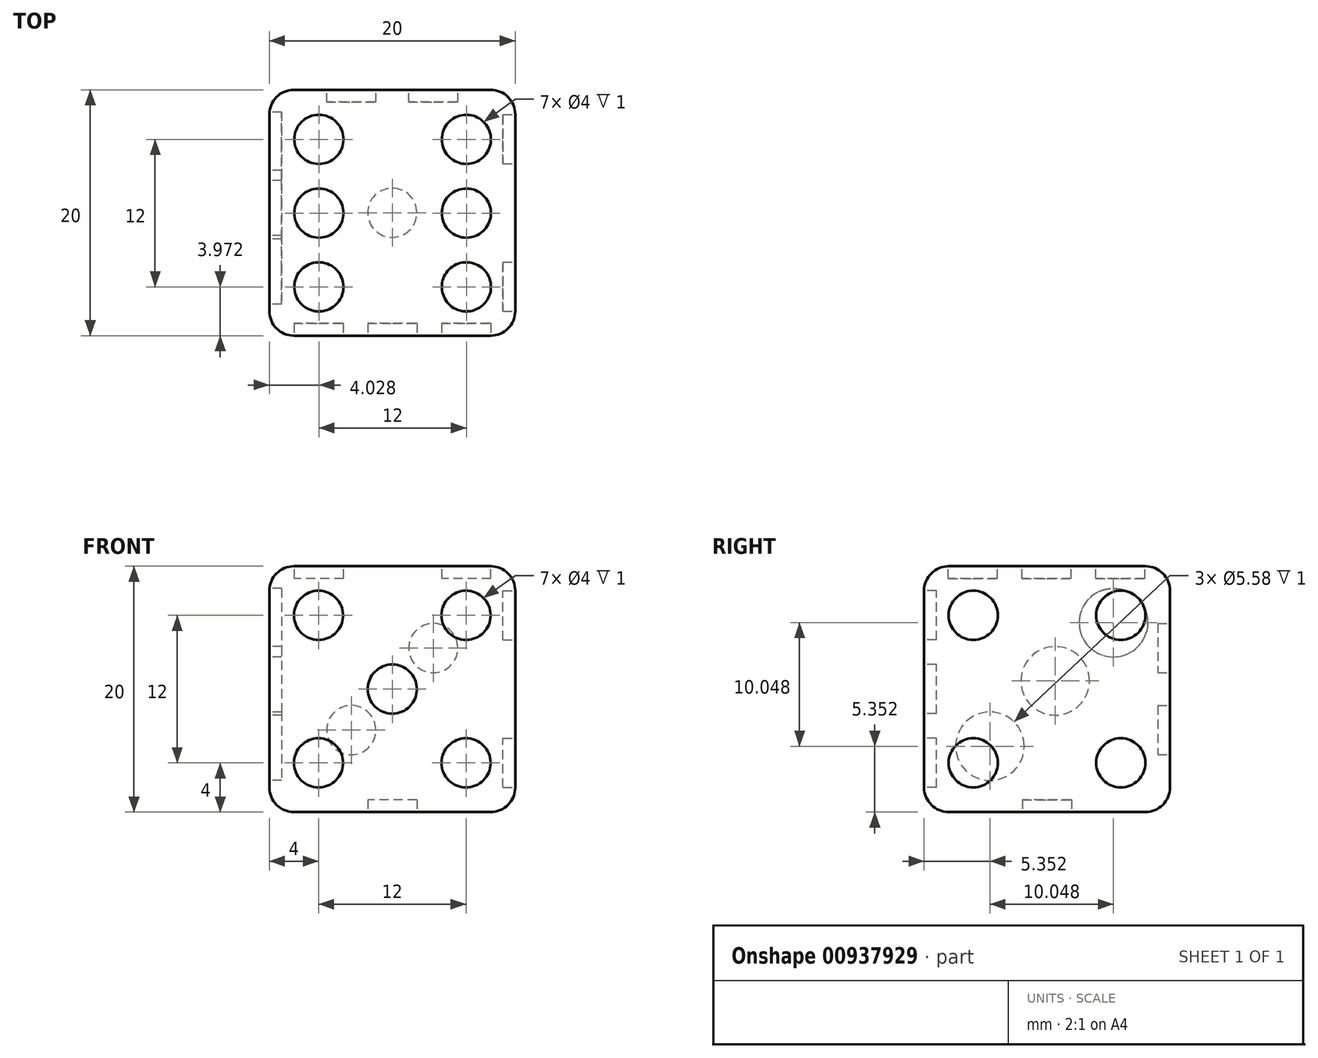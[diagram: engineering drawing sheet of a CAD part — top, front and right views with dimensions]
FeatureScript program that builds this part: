
annotation { "Feature Type Name" : "Feature", "Feature Type Description" : "" }
export const myFeature = defineFeature(function(context is Context, id is Id, definition is map)
    precondition{}
    {
        {
            var Q0;
            Q0=qCreatedBy(makeId("Top.planeOp"),FACE);
            var sketch = newSketch(context, id + "F0", { "sketchPlane" : qUnion([Q0])});
            skLineSegment(sketch, "E0.bottom", {"start": v(0, 0) * mm, "end": v(20, 0) * mm});
            skLineSegment(sketch, "E0.top", {"start": v(0, 20) * mm, "end": v(20, 20) * mm});
            skLineSegment(sketch, "E0.left", {"start": v(0, 0) * mm, "end": v(0, 20) * mm});
            skLineSegment(sketch, "E0.right", {"start": v(20, 0) * mm, "end": v(20, 20) * mm});
            skSolve(sketch);
        }
        {
            var Q0;
            Q0 = qSketchRegion(id + "F0", true);
            extrude(context, id + "F1", {"entities" : qUnion([Q0]), "depth" : 20 * mm, "offsetDistance" : 25 * mm});
        }
        {
            var Q0;
            Q0=qCreatedBy(makeId("Top.planeOp"),FACE);
            var sketch = newSketch(context, id + "F2", { "sketchPlane" : qUnion([Q0])});
            skCircle(sketch, "E1", {"center": v(10, 10) * mm, "radius": 2 * mm});
            skLineSegment(sketch, "E2.0.0", {"start": v(20, 20) * mm, "end": v(0, 20) * mm});
            skLineSegment(sketch, "E2.0.1", {"start": v(0, 20) * mm, "end": v(0, 0) * mm});
            skLineSegment(sketch, "E2.0.2", {"start": v(0, 0) * mm, "end": v(20, 0) * mm});
            skLineSegment(sketch, "E2.0.3", {"start": v(20, 0) * mm, "end": v(20, 20) * mm});
            skLineSegment(sketch, "E3", {"start": v(20, 20) * mm, "end": v(0, 0) * mm, "construction": true});
            skLineSegment(sketch, "E4", {"start": v(0, 20) * mm, "end": v(20, 0) * mm, "construction": true});
            skSolve(sketch);
        }
        {
            var Q0;
            Q0=makeQuery(id+"F1.opExtrude","CAP_FACE",FACE,{"disambiguationData":[OSD([sQuery(id+"F0.wireOp",EDGE,"E0.bottom"),sQuery(id+"F0.wireOp",EDGE,"E0.top"),sQuery(id+"F0.wireOp",EDGE,"E0.left"),sQuery(id+"F0.wireOp",EDGE,"E0.right")])],"isStart":false});
            var sketch = newSketch(context, id + "F3", { "sketchPlane" : qUnion([Q0])});
            skLineSegment(sketch, "E5", {"start": v(20, 20) * mm, "end": v(0, 0) * mm, "construction": true});
            skLineSegment(sketch, "E6", {"start": v(0, 20) * mm, "end": v(20, 0) * mm, "construction": true});
            skLineSegment(sketch, "E7.bottom", {"start": v(4.03, 15.97) * mm, "end": v(16.03, 15.97) * mm, "construction": true});
            skLineSegment(sketch, "E7.top", {"start": v(4.03, 3.97) * mm, "end": v(16.03, 3.97) * mm, "construction": true});
            skLineSegment(sketch, "E7.left", {"start": v(4.03, 15.97) * mm, "end": v(4.03, 3.97) * mm, "construction": true});
            skLineSegment(sketch, "E7.right", {"start": v(16.03, 15.97) * mm, "end": v(16.03, 3.97) * mm, "construction": true});
            skCircle(sketch, "E8", {"center": v(4.03, 15.97) * mm, "radius": 2 * mm});
            skCircle(sketch, "E9", {"center": v(4.03, 3.97) * mm, "radius": 2 * mm});
            skCircle(sketch, "E10", {"center": v(16.03, 3.97) * mm, "radius": 2 * mm});
            skCircle(sketch, "E11", {"center": v(16.03, 15.97) * mm, "radius": 2 * mm});
            skCircle(sketch, "E12", {"center": v(16.03, 9.97) * mm, "radius": 2 * mm});
            skCircle(sketch, "E13", {"center": v(4.03, 9.97) * mm, "radius": 2 * mm});
            skSolve(sketch);
        }
        {
            var Q0;
            Q0=qCreatedBy(makeId("Front.planeOp"),FACE);
            var sketch = newSketch(context, id + "F4", { "sketchPlane" : qUnion([Q0])});
            skLineSegment(sketch, "E14", {"start": v(20, 0) * mm, "end": v(0, 20) * mm, "construction": true});
            skLineSegment(sketch, "E15", {"start": v(0, 0) * mm, "end": v(20, 20) * mm, "construction": true});
            skLineSegment(sketch, "E16.bottom", {"start": v(16, 16) * mm, "end": v(4, 16) * mm, "construction": true});
            skLineSegment(sketch, "E16.top", {"start": v(16, 4) * mm, "end": v(4, 4) * mm, "construction": true});
            skLineSegment(sketch, "E16.left", {"start": v(16, 16) * mm, "end": v(16, 4) * mm, "construction": true});
            skLineSegment(sketch, "E16.right", {"start": v(4, 16) * mm, "end": v(4, 4) * mm, "construction": true});
            skCircle(sketch, "E17", {"center": v(16, 4) * mm, "radius": 2 * mm});
            skCircle(sketch, "E18", {"center": v(4, 16) * mm, "radius": 2 * mm});
            skCircle(sketch, "E19", {"center": v(16, 16) * mm, "radius": 2 * mm});
            skCircle(sketch, "E20", {"center": v(4, 4) * mm, "radius": 2 * mm});
            skCircle(sketch, "E21", {"center": v(10, 10) * mm, "radius": 2 * mm});
            skSolve(sketch);
        }
        {
            var Q0;
            Q0=makeQuery(id+"F1.opExtrude","SWEPT_FACE",FACE,{"disambiguationData":[OSD([sQuery(id+"F0.wireOp",EDGE,"E0.top")])]});
            var sketch = newSketch(context, id + "F5", { "sketchPlane" : qUnion([Q0])});
            skCircle(sketch, "E22", {"center": v(-13.33, 13.33) * mm, "radius": 2 * mm});
            skCircle(sketch, "E23", {"center": v(-6.67, 6.67) * mm, "radius": 2 * mm});
            skLineSegment(sketch, "E24", {"start": v(-20, 20) * mm, "end": v(-13.33, 13.33) * mm, "construction": true});
            skLineSegment(sketch, "E25", {"start": v(-13.33, 13.33) * mm, "end": v(-6.67, 6.67) * mm, "construction": true});
            skLineSegment(sketch, "E26", {"start": v(-6.67, 6.67) * mm, "end": v(0, 0) * mm, "construction": true});
            skSolve(sketch);
        }
        {
            var Q0;
            Q0=makeQuery(id+"F1.opExtrude","SWEPT_FACE",FACE,{"disambiguationData":[OSD([sQuery(id+"F0.wireOp",EDGE,"E0.left")])]});
            var sketch = newSketch(context, id + "F6", { "sketchPlane" : qUnion([Q0])});
            skCircle(sketch, "E27", {"center": v(-15.4, 15.4) * mm, "radius": 2.79 * mm});
            skCircle(sketch, "E28", {"center": v(-10.67, 10.67) * mm, "radius": 2.79 * mm});
            skCircle(sketch, "E29", {"center": v(-5.35, 5.35) * mm, "radius": 2.79 * mm});
            skLineSegment(sketch, "E30", {"start": v(-20, 20) * mm, "end": v(-15.4, 15.4) * mm, "construction": true});
            skLineSegment(sketch, "E31", {"start": v(-15.4, 15.4) * mm, "end": v(-10.67, 10.67) * mm, "construction": true});
            skLineSegment(sketch, "E32", {"start": v(-10.67, 10.67) * mm, "end": v(-5.35, 5.35) * mm, "construction": true});
            skLineSegment(sketch, "E33", {"start": v(-5.35, 5.35) * mm, "end": v(0, 0) * mm, "construction": true});
            skSolve(sketch);
        }
        {
            var Q0;
            Q0=makeQuery(id+"F1.opExtrude","SWEPT_FACE",FACE,{"disambiguationData":[OSD([sQuery(id+"F0.wireOp",EDGE,"E0.right")])]});
            var sketch = newSketch(context, id + "F7", { "sketchPlane" : qUnion([Q0])});
            skLineSegment(sketch, "E34", {"start": v(20, 20) * mm, "end": v(0, 0) * mm, "construction": true});
            skLineSegment(sketch, "E35", {"start": v(0, 20) * mm, "end": v(20, 0) * mm, "construction": true});
            skLineSegment(sketch, "E36.bottom", {"start": v(4, 16) * mm, "end": v(16, 16) * mm, "construction": true});
            skLineSegment(sketch, "E36.top", {"start": v(4, 4) * mm, "end": v(16, 4) * mm, "construction": true});
            skLineSegment(sketch, "E36.left", {"start": v(4, 16) * mm, "end": v(4, 4) * mm, "construction": true});
            skLineSegment(sketch, "E36.right", {"start": v(16, 16) * mm, "end": v(16, 4) * mm, "construction": true});
            skCircle(sketch, "E37", {"center": v(4, 16) * mm, "radius": 2 * mm});
            skCircle(sketch, "E38", {"center": v(4, 4) * mm, "radius": 2 * mm});
            skCircle(sketch, "E39", {"center": v(16, 4) * mm, "radius": 2 * mm});
            skCircle(sketch, "E40", {"center": v(16, 16) * mm, "radius": 2 * mm});
            skSolve(sketch);
        }
        {
            var Q0;
            Q0=makeQuery(id+"F3.imprint","IMPRINT",FACE,{"disambiguationData":[TD([[makeQuery(id+"F3.imprint","IMPRINT",EDGE,{"derivedFrom":sQuery(id+"F3.wireOp",EDGE,"E8")}),1.0]])]});
            var Q1;
            Q1=makeQuery(id+"F3.imprint","IMPRINT",FACE,{"disambiguationData":[TD([[makeQuery(id+"F3.imprint","IMPRINT",EDGE,{"derivedFrom":sQuery(id+"F3.wireOp",EDGE,"E13")}),1.0]])]});
            var Q2;
            Q2=makeQuery(id+"F3.imprint","IMPRINT",FACE,{"disambiguationData":[TD([[makeQuery(id+"F3.imprint","IMPRINT",EDGE,{"derivedFrom":sQuery(id+"F3.wireOp",EDGE,"E9")}),1.0]])]});
            var Q3;
            Q3=makeQuery(id+"F3.imprint","IMPRINT",FACE,{"disambiguationData":[TD([[makeQuery(id+"F3.imprint","IMPRINT",EDGE,{"derivedFrom":sQuery(id+"F3.wireOp",EDGE,"E11")}),1.0]])]});
            var Q4;
            Q4=makeQuery(id+"F3.imprint","IMPRINT",FACE,{"disambiguationData":[TD([[makeQuery(id+"F3.imprint","IMPRINT",EDGE,{"derivedFrom":sQuery(id+"F3.wireOp",EDGE,"E12")}),1.0]])]});
            var Q5;
            Q5=makeQuery(id+"F3.imprint","IMPRINT",FACE,{"disambiguationData":[TD([[makeQuery(id+"F3.imprint","IMPRINT",EDGE,{"derivedFrom":sQuery(id+"F3.wireOp",EDGE,"E10")}),1.0]])]});
            extrude(context, id + "F8", {"entities" : qUnion([Q0, Q1, Q2, Q3, Q4, Q5]), "operationType" : NewBodyOperationType.REMOVE, "oppositeDirection" : true, "depth" : 1 * mm, "offsetDistance" : 25 * mm});
        }
        {
            var Q0;
            {var subQ0=sQuery(id+"F2.wireOp",EDGE,"DLmDA1Jz-B1Br-PbYC-twxk-7bfob2sfivJC");var subQ1=sQuery(id+"F2.wireOp",EDGE,"E1");var subQ2=makeQuery(id+"F2.imprint","INTERSECT",VERTEX,{"disambiguationData":[OD(0.0)],"derivedFrom":[subQ1,subQ0]});Q0=makeQuery(id+"F2.imprint","IMPRINT",FACE,{"disambiguationData":[TD([[makeQuery(id+"F2.imprint","IMPRINT",EDGE,{"disambiguationData":[TD([[subQ2,1.0]])],"derivedFrom":subQ1}),1.0]])]});}
            var Q1;
            {var subQ0=sQuery(id+"F2.wireOp",EDGE,"DLmDA1Jz-B1Br-PbYC-twxk-7bfob2sfivJC");var subQ1=sQuery(id+"F2.wireOp",EDGE,"E1");var subQ2=makeQuery(id+"F2.imprint","INTERSECT",VERTEX,{"disambiguationData":[OD(0.0)],"derivedFrom":[subQ1,subQ0]});Q1=makeQuery(id+"F2.imprint","IMPRINT",FACE,{"disambiguationData":[TD([[makeQuery(id+"F2.imprint","IMPRINT",EDGE,{"disambiguationData":[TD([[subQ2,-1.0]])],"derivedFrom":subQ1}),1.0]])]});}
            var Q2;
            {var subQ0=sQuery(id+"F2.wireOp",EDGE,"LqWkyFCt-tRJL-dN5y-AN8d-2VUP0lAdGxYt");var subQ1=sQuery(id+"F2.wireOp",EDGE,"E1");var subQ2=makeQuery(id+"F2.imprint","INTERSECT",VERTEX,{"disambiguationData":[OD(0.0)],"derivedFrom":[subQ1,subQ0]});Q2=makeQuery(id+"F2.imprint","IMPRINT",FACE,{"disambiguationData":[TD([[makeQuery(id+"F2.imprint","IMPRINT",EDGE,{"disambiguationData":[TD([[subQ2,1.0]])],"derivedFrom":subQ1}),1.0]])]});}
            var Q3;
            {var subQ0=sQuery(id+"F2.wireOp",EDGE,"LqWkyFCt-tRJL-dN5y-AN8d-2VUP0lAdGxYt");var subQ1=sQuery(id+"F2.wireOp",EDGE,"E1");var subQ2=makeQuery(id+"F2.imprint","INTERSECT",VERTEX,{"disambiguationData":[OD(1.0)],"derivedFrom":[subQ1,subQ0]});Q3=makeQuery(id+"F2.imprint","IMPRINT",FACE,{"disambiguationData":[TD([[makeQuery(id+"F2.imprint","IMPRINT",EDGE,{"disambiguationData":[TD([[subQ2,-1.0]])],"derivedFrom":subQ1}),1.0]])]});}
            var Q4;
            Q4=sQuery(id+"F2.wireOp",EDGE,"E1");
            extrude(context, id + "F9", {"entities" : qUnion([Q0, Q1, Q2, Q3]), "operationType" : NewBodyOperationType.REMOVE, "surfaceEntities" : qUnion([Q4]), "oppositeDirection" : true, "depth" : 1 * mm, "offsetDistance" : 25 * mm});
        }
        {
            var Q0;
            {var subQ0=sQuery(id+"F2.wireOp",EDGE,"LqWkyFCt-tRJL-dN5y-AN8d-2VUP0lAdGxYt");var subQ1=sQuery(id+"F2.wireOp",EDGE,"E1");var subQ2=makeQuery(id+"F2.imprint","INTERSECT",VERTEX,{"disambiguationData":[OD(0.0)],"derivedFrom":[subQ1,subQ0]});Q0=makeQuery(id+"F2.imprint","IMPRINT",FACE,{"disambiguationData":[TD([[makeQuery(id+"F2.imprint","IMPRINT",EDGE,{"disambiguationData":[TD([[subQ2,1.0]])],"derivedFrom":subQ1}),1.0]])]});}
            var Q1;
            {var subQ0=sQuery(id+"F2.wireOp",EDGE,"DLmDA1Jz-B1Br-PbYC-twxk-7bfob2sfivJC");var subQ1=sQuery(id+"F2.wireOp",EDGE,"E1");var subQ2=makeQuery(id+"F2.imprint","INTERSECT",VERTEX,{"disambiguationData":[OD(0.0)],"derivedFrom":[subQ1,subQ0]});Q1=makeQuery(id+"F2.imprint","IMPRINT",FACE,{"disambiguationData":[TD([[makeQuery(id+"F2.imprint","IMPRINT",EDGE,{"disambiguationData":[TD([[subQ2,1.0]])],"derivedFrom":subQ1}),1.0]])]});}
            var Q2;
            {var subQ0=sQuery(id+"F2.wireOp",EDGE,"LqWkyFCt-tRJL-dN5y-AN8d-2VUP0lAdGxYt");var subQ1=sQuery(id+"F2.wireOp",EDGE,"E1");var subQ2=makeQuery(id+"F2.imprint","INTERSECT",VERTEX,{"disambiguationData":[OD(1.0)],"derivedFrom":[subQ1,subQ0]});Q2=makeQuery(id+"F2.imprint","IMPRINT",FACE,{"disambiguationData":[TD([[makeQuery(id+"F2.imprint","IMPRINT",EDGE,{"disambiguationData":[TD([[subQ2,-1.0]])],"derivedFrom":subQ1}),1.0]])]});}
            var Q3;
            {var subQ0=sQuery(id+"F2.wireOp",EDGE,"DLmDA1Jz-B1Br-PbYC-twxk-7bfob2sfivJC");var subQ1=sQuery(id+"F2.wireOp",EDGE,"E1");var subQ2=makeQuery(id+"F2.imprint","INTERSECT",VERTEX,{"disambiguationData":[OD(0.0)],"derivedFrom":[subQ1,subQ0]});Q3=makeQuery(id+"F2.imprint","IMPRINT",FACE,{"disambiguationData":[TD([[makeQuery(id+"F2.imprint","IMPRINT",EDGE,{"disambiguationData":[TD([[subQ2,-1.0]])],"derivedFrom":subQ1}),1.0]])]});}
            var Q4;
            Q4=sQuery(id+"F2.wireOp",EDGE,"E1");
            extrude(context, id + "F10", {"entities" : qUnion([Q0, Q1, Q2, Q3]), "operationType" : NewBodyOperationType.REMOVE, "surfaceEntities" : qUnion([Q4]), "oppositeDirection" : true, "depth" : 1 * mm, "offsetDistance" : 25 * mm});
        }
        {
            var Q0;
            Q0=makeQuery(id+"F2.imprint","IMPRINT",FACE,{"disambiguationData":[TD([[makeQuery(id+"F2.imprint","IMPRINT",EDGE,{"derivedFrom":sQuery(id+"F2.wireOp",EDGE,"E1")}),1.0]])]});
            extrude(context, id + "F11", {"entities" : qUnion([Q0]), "operationType" : NewBodyOperationType.REMOVE, "depth" : 1 * mm, "offsetDistance" : 25 * mm});
        }
        {
            var Q0;
            Q0=makeQuery(id+"F6.imprint","IMPRINT",FACE,{"disambiguationData":[TD([[makeQuery(id+"F6.imprint","IMPRINT",EDGE,{"derivedFrom":sQuery(id+"F6.wireOp",EDGE,"E27")}),1.0]])]});
            var Q1;
            Q1=makeQuery(id+"F6.imprint","IMPRINT",FACE,{"disambiguationData":[TD([[makeQuery(id+"F6.imprint","IMPRINT",EDGE,{"derivedFrom":sQuery(id+"F6.wireOp",EDGE,"E28")}),1.0]])]});
            var Q2;
            Q2=makeQuery(id+"F6.imprint","IMPRINT",FACE,{"disambiguationData":[TD([[makeQuery(id+"F6.imprint","IMPRINT",EDGE,{"derivedFrom":sQuery(id+"F6.wireOp",EDGE,"E29")}),1.0]])]});
            extrude(context, id + "F12", {"entities" : qUnion([Q0, Q1, Q2]), "operationType" : NewBodyOperationType.REMOVE, "oppositeDirection" : true, "depth" : 1 * mm, "offsetDistance" : 25 * mm});
        }
        {
            var Q0;
            Q0 = qSketchRegion(id + "F4", true);
            extrude(context, id + "F13", {"entities" : qUnion([Q0]), "operationType" : NewBodyOperationType.REMOVE, "oppositeDirection" : true, "depth" : 1 * mm, "offsetDistance" : 25 * mm});
        }
        {
            var Q0;
            Q0=makeQuery(id+"F6.imprint","IMPRINT",FACE,{"disambiguationData":[TD([[makeQuery(id+"F6.imprint","IMPRINT",EDGE,{"derivedFrom":sQuery(id+"F6.wireOp",EDGE,"E27")}),1.0]])]});
            var Q1;
            Q1=makeQuery(id+"F6.imprint","IMPRINT",FACE,{"disambiguationData":[TD([[makeQuery(id+"F6.imprint","IMPRINT",EDGE,{"derivedFrom":sQuery(id+"F6.wireOp",EDGE,"E28")}),1.0]])]});
            var Q2;
            Q2=makeQuery(id+"F6.imprint","IMPRINT",FACE,{"disambiguationData":[TD([[makeQuery(id+"F6.imprint","IMPRINT",EDGE,{"derivedFrom":sQuery(id+"F6.wireOp",EDGE,"E29")}),1.0]])]});
            var Q3;
            Q3=sQuery(id+"F6.wireOp",EDGE,"E27");
            var Q4;
            Q4=sQuery(id+"F6.wireOp",EDGE,"E28");
            var Q5;
            Q5=sQuery(id+"F6.wireOp",EDGE,"E29");
            extrude(context, id + "F14", {"entities" : qUnion([Q0, Q1, Q2]), "operationType" : NewBodyOperationType.REMOVE, "surfaceEntities" : qUnion([Q3, Q4, Q5]), "oppositeDirection" : true, "depth" : 1 * mm, "offsetDistance" : 25 * mm});
        }
        {
            var Q0;
            Q0 = qSketchRegion(id + "F5", true);
            extrude(context, id + "F15", {"entities" : qUnion([Q0]), "operationType" : NewBodyOperationType.REMOVE, "oppositeDirection" : true, "depth" : 1 * mm, "offsetDistance" : 25 * mm});
        }
        {
            var Q0;
            Q0=makeQuery(id+"F7.imprint","IMPRINT",FACE,{"disambiguationData":[TD([[makeQuery(id+"F7.imprint","IMPRINT",EDGE,{"derivedFrom":sQuery(id+"F7.wireOp",EDGE,"E39")}),1.0]])]});
            var Q1;
            Q1=makeQuery(id+"F7.imprint","IMPRINT",FACE,{"disambiguationData":[TD([[makeQuery(id+"F7.imprint","IMPRINT",EDGE,{"derivedFrom":sQuery(id+"F7.wireOp",EDGE,"E40")}),1.0]])]});
            var Q2;
            Q2=makeQuery(id+"F7.imprint","IMPRINT",FACE,{"disambiguationData":[TD([[makeQuery(id+"F7.imprint","IMPRINT",EDGE,{"derivedFrom":sQuery(id+"F7.wireOp",EDGE,"E37")}),1.0]])]});
            var Q3;
            Q3=makeQuery(id+"F7.imprint","IMPRINT",FACE,{"disambiguationData":[TD([[makeQuery(id+"F7.imprint","IMPRINT",EDGE,{"derivedFrom":sQuery(id+"F7.wireOp",EDGE,"E38")}),1.0]])]});
            extrude(context, id + "F16", {"entities" : qUnion([Q0, Q1, Q2, Q3]), "operationType" : NewBodyOperationType.REMOVE, "oppositeDirection" : true, "depth" : 1 * mm, "offsetDistance" : 25 * mm});
        }
        {
            var Q0;
            Q0=makeQuery(id+"F1.opExtrude","CAP_EDGE",EDGE,{"disambiguationData":[OSD([sQuery(id+"F0.wireOp",EDGE,"E0.top")])],"isStart":true});
            var Q1;
            Q1=makeQuery(id+"F1.opExtrude","CAP_EDGE",EDGE,{"disambiguationData":[OSD([sQuery(id+"F0.wireOp",EDGE,"E0.right")])],"isStart":true});
            var Q2;
            Q2=makeQuery(id+"F1.opExtrude","CAP_EDGE",EDGE,{"disambiguationData":[OSD([sQuery(id+"F0.wireOp",EDGE,"E0.bottom")])],"isStart":true});
            var Q3;
            Q3=makeQuery(id+"F1.opExtrude","CAP_EDGE",EDGE,{"disambiguationData":[OSD([sQuery(id+"F0.wireOp",EDGE,"E0.left")])],"isStart":true});
            var Q4;
            Q4=makeQuery(id+"F1.opExtrude","SWEPT_EDGE",EDGE,{"disambiguationData":[OSD([sQuery(id+"F0.wireOp",EDGE,"E0.bottom"),sQuery(id+"F0.wireOp",EDGE,"E0.left")])]});
            var Q5;
            Q5=makeQuery(id+"F1.opExtrude","CAP_EDGE",EDGE,{"disambiguationData":[OSD([sQuery(id+"F0.wireOp",EDGE,"E0.left")])],"isStart":false});
            var Q6;
            Q6=makeQuery(id+"F1.opExtrude","SWEPT_EDGE",EDGE,{"disambiguationData":[OSD([sQuery(id+"F0.wireOp",EDGE,"E0.top"),sQuery(id+"F0.wireOp",EDGE,"E0.left")])]});
            var Q7;
            Q7=makeQuery(id+"F1.opExtrude","CAP_EDGE",EDGE,{"disambiguationData":[OSD([sQuery(id+"F0.wireOp",EDGE,"E0.bottom")])],"isStart":false});
            var Q8;
            Q8=makeQuery(id+"F1.opExtrude","SWEPT_EDGE",EDGE,{"disambiguationData":[OSD([sQuery(id+"F0.wireOp",EDGE,"E0.bottom"),sQuery(id+"F0.wireOp",EDGE,"E0.right")])]});
            var Q9;
            Q9=makeQuery(id+"F1.opExtrude","CAP_EDGE",EDGE,{"disambiguationData":[OSD([sQuery(id+"F0.wireOp",EDGE,"E0.right")])],"isStart":false});
            var Q10;
            Q10=makeQuery(id+"F1.opExtrude","CAP_EDGE",EDGE,{"disambiguationData":[OSD([sQuery(id+"F0.wireOp",EDGE,"E0.top")])],"isStart":false});
            var Q11;
            Q11=makeQuery(id+"F1.opExtrude","SWEPT_EDGE",EDGE,{"disambiguationData":[OSD([sQuery(id+"F0.wireOp",EDGE,"E0.top"),sQuery(id+"F0.wireOp",EDGE,"E0.right")])]});
            fillet(context, id + "F17", {"entities" : qUnion([Q0, Q1, Q2, Q3, Q4, Q5, Q6, Q7, Q8, Q9, Q10, Q11]), "radius" : 2 * mm, "tangentPropagation" : true, "allowEdgeOverflow" : false});
        }
    });
